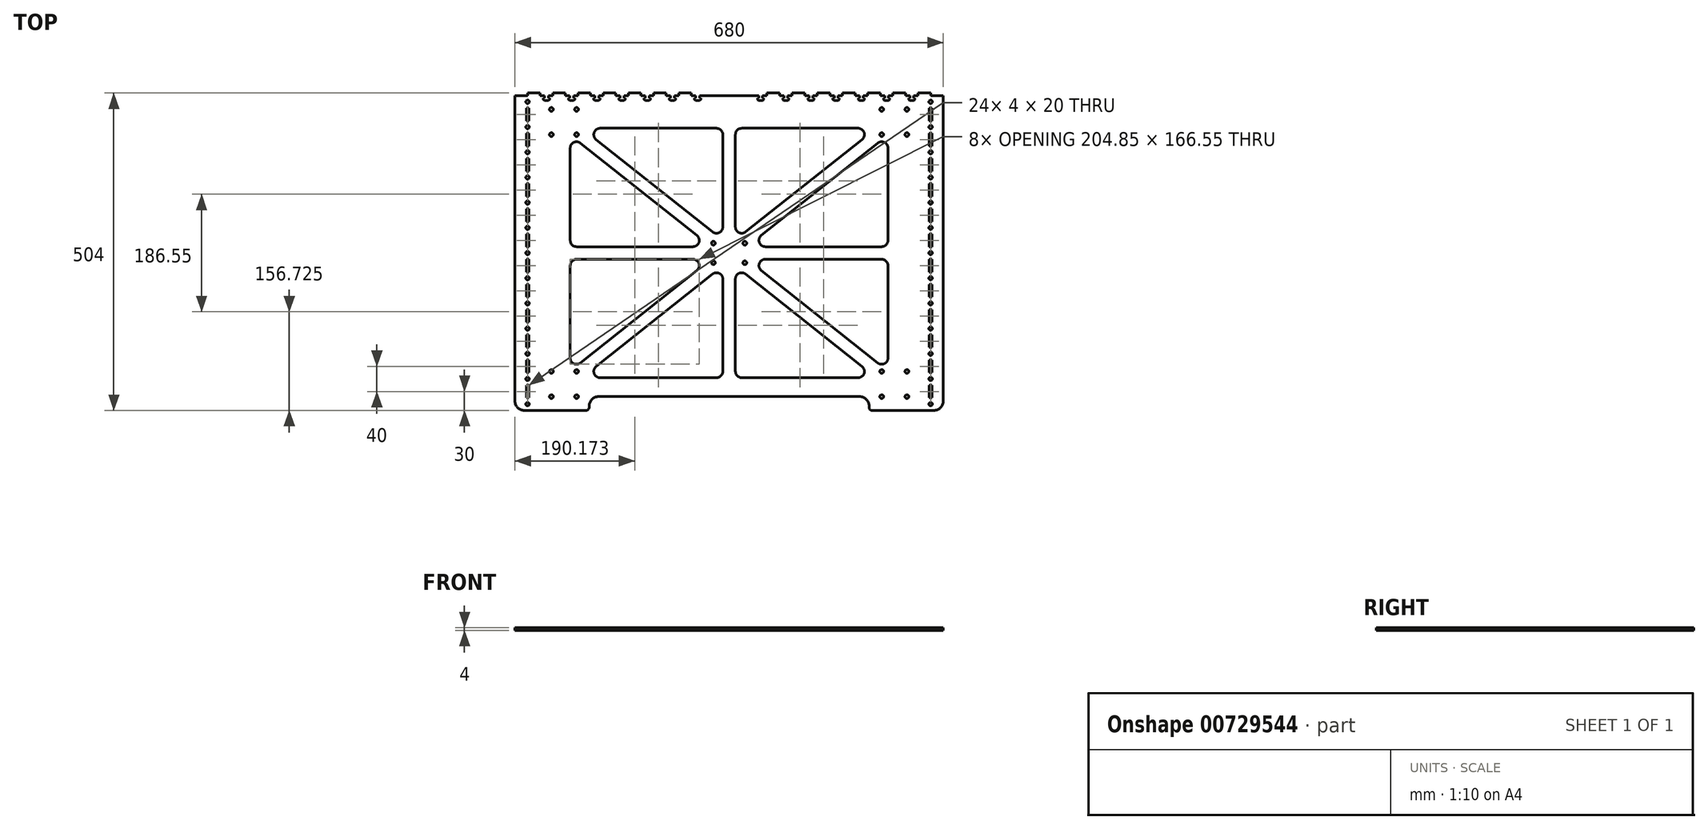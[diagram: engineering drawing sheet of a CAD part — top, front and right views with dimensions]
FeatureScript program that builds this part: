
annotation { "Feature Type Name" : "Feature", "Feature Type Description" : "" }
export const myFeature = defineFeature(function(context is Context, id is Id, definition is map)
    precondition{}
    {
        {
            var Q0;
            Q0=qCreatedBy(makeId("Top.planeOp"),FACE);
            var sketch = newSketch(context, id + "F0", { "sketchPlane" : qUnion([Q0])});
            skLineSegment(sketch, "E0.bottom", {"start": v(-340, 250) * mm, "end": v(-320, 250) * mm});
            skLineSegment(sketch, "E0.top", {"start": v(-325, -250) * mm, "end": v(-262.25, -250) * mm});
            skLineSegment(sketch, "E0.left", {"start": v(-340, 250) * mm, "end": v(-340, -235) * mm});
            skLineSegment(sketch, "E0.right", {"start": v(340, 250) * mm, "end": v(340, -235) * mm});
            skPoint(sketch, "E0.middle", {"position": v(0, 0) * mm});
            skLineSegment(sketch, "E1", {"start": v(-262.25, 250) * mm, "end": v(-262.25, -250) * mm, "construction": true});
            skLineSegment(sketch, "E2", {"start": v(262.25, 250) * mm, "end": v(262.25, -250) * mm, "construction": true});
            skLineSegment(sketch, "E3", {"start": v(0, -250) * mm, "end": v(0, 250) * mm, "construction": true});
            skLineSegment(sketch, "E4", {"start": v(340, 0) * mm, "end": v(-340, 0) * mm, "construction": true});
            skLineSegment(sketch, "E5.bottom", {"start": v(-282.25, -188) * mm, "end": v(-242.25, -188) * mm, "construction": true});
            skLineSegment(sketch, "E5.top", {"start": v(-282.25, -228) * mm, "end": v(-242.25, -228) * mm, "construction": true});
            skLineSegment(sketch, "E5.left", {"start": v(-282.25, -188) * mm, "end": v(-282.25, -228) * mm, "construction": true});
            skLineSegment(sketch, "E5.right", {"start": v(-242.25, -188) * mm, "end": v(-242.25, -228) * mm, "construction": true});
            skPoint(sketch, "E5.middle", {"position": v(-262.25, -208) * mm});
            skCircle(sketch, "E6", {"center": v(-242.25, -188) * mm, "radius": 3 * mm});
            skCircle(sketch, "E7.MirrorC", {"center": v(-282.25, -188) * mm, "radius": 3 * mm});
            skLineSegment(sketch, "E8", {"start": v(-282.25, -208) * mm, "end": v(262.25, -208) * mm, "construction": true});
            skCircle(sketch, "E9.MirrorC", {"center": v(-242.25, -228) * mm, "radius": 3 * mm});
            skCircle(sketch, "E10.MirrorC", {"center": v(-282.25, -228) * mm, "radius": 3 * mm});
            skCircle(sketch, "E11.MirrorC", {"center": v(-282.25, 188) * mm, "radius": 3 * mm});
            skCircle(sketch, "E12.MirrorC", {"center": v(-242.25, 188) * mm, "radius": 3 * mm});
            skCircle(sketch, "E13.MirrorC", {"center": v(-282.25, 228) * mm, "radius": 3 * mm});
            skCircle(sketch, "E14.MirrorC", {"center": v(-242.25, 228) * mm, "radius": 3 * mm});
            skCircle(sketch, "E15.MirrorC", {"center": v(282.25, 228) * mm, "radius": 3 * mm});
            skCircle(sketch, "E16.MirrorC", {"center": v(282.25, 188) * mm, "radius": 3 * mm});
            skCircle(sketch, "E17.MirrorC", {"center": v(242.25, 228) * mm, "radius": 3 * mm});
            skCircle(sketch, "E18.MirrorC", {"center": v(242.25, 188) * mm, "radius": 3 * mm});
            skCircle(sketch, "E19.MirrorC", {"center": v(282.25, -188) * mm, "radius": 3 * mm});
            skCircle(sketch, "E20.MirrorC", {"center": v(242.25, -188) * mm, "radius": 3 * mm});
            skCircle(sketch, "E21.MirrorC", {"center": v(242.25, -228) * mm, "radius": 3 * mm});
            skCircle(sketch, "E22.MirrorC", {"center": v(282.25, -228) * mm, "radius": 3 * mm});
            skPoint(sketch, "E23.visualSharp", {"position": v(-340, 250) * mm});
            skPoint(sketch, "E24.visualSharp", {"position": v(340, -250) * mm});
            skArc(sketch, "E24.filletArc", {"start": v(325, -250) * mm, "mid": v(335.6, -245.6) * mm, "end": v(340, -235) * mm});
            skPoint(sketch, "E25.visualSharp", {"position": v(340, 250) * mm});
            skPoint(sketch, "E26.visualSharp", {"position": v(-340, -250) * mm});
            skArc(sketch, "E26.filletArc", {"start": v(-340, -235) * mm, "mid": v(-335.6, -245.6) * mm, "end": v(-325, -250) * mm});
            skLineSegment(sketch, "E27.bottom", {"start": v(25, 15.5) * mm, "end": v(-25, 15.5) * mm, "construction": true});
            skLineSegment(sketch, "E27.top", {"start": v(25, -15.5) * mm, "end": v(-25, -15.5) * mm, "construction": true});
            skLineSegment(sketch, "E27.left", {"start": v(25, 15.5) * mm, "end": v(25, -15.5) * mm, "construction": true});
            skLineSegment(sketch, "E27.right", {"start": v(-25, 15.5) * mm, "end": v(-25, -15.5) * mm, "construction": true});
            skCircle(sketch, "E28", {"center": v(25, 15.5) * mm, "radius": 3 * mm});
            skLineSegment(sketch, "E29", {"start": v(25, 0) * mm, "end": v(0, 0) * mm, "construction": true});
            skCircle(sketch, "E30.MirrorC", {"center": v(25, -15.5) * mm, "radius": 3 * mm});
            skCircle(sketch, "E31.MirrorC", {"center": v(-25, 15.5) * mm, "radius": 3 * mm});
            skCircle(sketch, "E32.MirrorC", {"center": v(-25, -15.5) * mm, "radius": 3 * mm});
            skLineSegment(sketch, "E33", {"start": v(-262.25, -208) * mm, "end": v(0, 0) * mm, "construction": true});
            skLineSegment(sketch, "E34", {"start": v(-242.25, -10) * mm, "end": v(-57.4, -10) * mm});
            skLineSegment(sketch, "E35", {"start": v(-51.19, -27.83) * mm, "end": v(-236.04, -174.45) * mm});
            skLineSegment(sketch, "E36", {"start": v(-252.25, -166.61) * mm, "end": v(-252.25, -20) * mm});
            skPoint(sketch, "E37.visualSharp", {"position": v(-252.25, -10) * mm});
            skArc(sketch, "E37.filletArc", {"start": v(-242.25, -10) * mm, "mid": v(-249.32, -12.93) * mm, "end": v(-252.25, -20) * mm});
            skPoint(sketch, "E38.visualSharp", {"position": v(-252.25, -187.3) * mm});
            skArc(sketch, "E38.filletArc", {"start": v(-252.25, -166.61) * mm, "mid": v(-246.6, -175.61) * mm, "end": v(-236.04, -174.45) * mm});
            skPoint(sketch, "E39.visualSharp", {"position": v(-28.7, -10) * mm});
            skArc(sketch, "E39.filletArc", {"start": v(-51.19, -27.83) * mm, "mid": v(-47.96, -16.7) * mm, "end": v(-57.4, -10) * mm});
            skPoint(sketch, "E40.orphan", {"position": v(-242.25, -208) * mm});
            skLineSegment(sketch, "E41", {"start": v(-320, 250) * mm, "end": v(-320, -250) * mm, "construction": true});
            skLineSegment(sketch, "E42.bottom", {"start": v(-318, 210) * mm, "end": v(-322, 210) * mm});
            skLineSegment(sketch, "E42.top", {"start": v(-318, 230) * mm, "end": v(-322, 230) * mm});
            skLineSegment(sketch, "E42.left", {"start": v(-318, 210) * mm, "end": v(-318, 230) * mm});
            skLineSegment(sketch, "E42.right", {"start": v(-322, 210) * mm, "end": v(-322, 230) * mm});
            skPoint(sketch, "E42.middle", {"position": v(-320, 220) * mm});
            skCircle(sketch, "E43", {"center": v(-320, 240) * mm, "radius": 2.75 * mm});
            skCircle(sketch, "E44.0.1.0", {"center": v(-320, 200) * mm, "radius": 2.75 * mm});
            skLineSegment(sketch, "E44.0.1.1", {"start": v(-322, 170) * mm, "end": v(-322, 190) * mm});
            skLineSegment(sketch, "E44.0.1.2", {"start": v(-318, 190) * mm, "end": v(-322, 190) * mm});
            skPoint(sketch, "E44.0.1.3", {"position": v(-320, 180) * mm});
            skLineSegment(sketch, "E44.0.1.4", {"start": v(-318, 170) * mm, "end": v(-318, 190) * mm});
            skLineSegment(sketch, "E44.0.1.5", {"start": v(-318, 170) * mm, "end": v(-322, 170) * mm});
            skCircle(sketch, "E44.0.2.0", {"center": v(-320, 160) * mm, "radius": 2.75 * mm});
            skLineSegment(sketch, "E44.0.2.1", {"start": v(-322, 130) * mm, "end": v(-322, 150) * mm});
            skLineSegment(sketch, "E44.0.2.2", {"start": v(-318, 150) * mm, "end": v(-322, 150) * mm});
            skPoint(sketch, "E44.0.2.3", {"position": v(-320, 140) * mm});
            skLineSegment(sketch, "E44.0.2.4", {"start": v(-318, 130) * mm, "end": v(-318, 150) * mm});
            skLineSegment(sketch, "E44.0.2.5", {"start": v(-318, 130) * mm, "end": v(-322, 130) * mm});
            skCircle(sketch, "E44.0.3.0", {"center": v(-320, 120) * mm, "radius": 2.75 * mm});
            skLineSegment(sketch, "E44.0.3.1", {"start": v(-322, 90) * mm, "end": v(-322, 110) * mm});
            skLineSegment(sketch, "E44.0.3.2", {"start": v(-318, 110) * mm, "end": v(-322, 110) * mm});
            skPoint(sketch, "E44.0.3.3", {"position": v(-320, 100) * mm});
            skLineSegment(sketch, "E44.0.3.4", {"start": v(-318, 90) * mm, "end": v(-318, 110) * mm});
            skLineSegment(sketch, "E44.0.3.5", {"start": v(-318, 90) * mm, "end": v(-322, 90) * mm});
            skCircle(sketch, "E44.0.4.0", {"center": v(-320, 80) * mm, "radius": 2.75 * mm});
            skLineSegment(sketch, "E44.0.4.1", {"start": v(-322, 50) * mm, "end": v(-322, 70) * mm});
            skLineSegment(sketch, "E44.0.4.2", {"start": v(-318, 70) * mm, "end": v(-322, 70) * mm});
            skPoint(sketch, "E44.0.4.3", {"position": v(-320, 60) * mm});
            skLineSegment(sketch, "E44.0.4.4", {"start": v(-318, 50) * mm, "end": v(-318, 70) * mm});
            skLineSegment(sketch, "E44.0.4.5", {"start": v(-318, 50) * mm, "end": v(-322, 50) * mm});
            skLineSegment(sketch, "E44.direction1", {"start": v(-320, 240) * mm, "end": v(-280, 240) * mm, "construction": true});
            skLineSegment(sketch, "E44.direction2", {"start": v(-320, 240) * mm, "end": v(-320, 200) * mm, "construction": true});
            skLineSegment(sketch, "E45.top", {"start": v(-320, 254) * mm, "end": v(-300, 254) * mm});
            skLineSegment(sketch, "E45.left", {"start": v(-320, 250) * mm, "end": v(-320, 254) * mm});
            skLineSegment(sketch, "E45.right", {"start": v(-300, 250) * mm, "end": v(-300, 254) * mm});
            skLineSegment(sketch, "E46.trimOffspring", {"start": v(-300, 250) * mm, "end": v(-293, 250) * mm});
            skLineSegment(sketch, "E47.MirrorCS", {"start": v(340, 250) * mm, "end": v(320, 250) * mm});
            skLineSegment(sketch, "E48.MirrorCS", {"start": v(320, 250) * mm, "end": v(320, -250) * mm, "construction": true});
            skPoint(sketch, "E49.orphan", {"position": v(0, 250) * mm});
            skPoint(sketch, "E50.orphan", {"position": v(-262.25, 250) * mm});
            skLineSegment(sketch, "E51", {"start": v(-26.21, -33.55) * mm, "end": v(-211.06, -180.17) * mm});
            skLineSegment(sketch, "E52", {"start": v(-204.85, -198) * mm, "end": v(-20, -198) * mm});
            skLineSegment(sketch, "E53", {"start": v(-10, -188) * mm, "end": v(-10, -41.39) * mm});
            skPoint(sketch, "E54.visualSharp", {"position": v(-10, -20.7) * mm});
            skArc(sketch, "E54.filletArc", {"start": v(-10, -41.39) * mm, "mid": v(-15.65, -32.39) * mm, "end": v(-26.21, -33.55) * mm});
            skPoint(sketch, "E55.visualSharp", {"position": v(-233.55, -198) * mm});
            skArc(sketch, "E55.filletArc", {"start": v(-211.06, -180.17) * mm, "mid": v(-214.3, -191.3) * mm, "end": v(-204.85, -198) * mm});
            skPoint(sketch, "E56.visualSharp", {"position": v(-10, -198) * mm});
            skArc(sketch, "E56.filletArc", {"start": v(-20, -198) * mm, "mid": v(-12.93, -195.07) * mm, "end": v(-10, -188) * mm});
            skLineSegment(sketch, "E57.MirrorCS", {"start": v(10, -188) * mm, "end": v(10, -41.39) * mm});
            skArc(sketch, "E58.MirrorCS", {"start": v(10, -41.39) * mm, "mid": v(15.65, -32.39) * mm, "end": v(26.21, -33.55) * mm});
            skArc(sketch, "E59.MirrorCS", {"start": v(20, -198) * mm, "mid": v(12.93, -195.07) * mm, "end": v(10, -188) * mm});
            skLineSegment(sketch, "E60.MirrorCS", {"start": v(204.85, -198) * mm, "end": v(20, -198) * mm});
            skArc(sketch, "E61.MirrorCS", {"start": v(211.06, -180.17) * mm, "mid": v(214.3, -191.3) * mm, "end": v(204.85, -198) * mm});
            skLineSegment(sketch, "E62.MirrorCS", {"start": v(26.21, -33.55) * mm, "end": v(211.06, -180.17) * mm});
            skLineSegment(sketch, "E63.MirrorCS", {"start": v(51.19, -27.83) * mm, "end": v(236.04, -174.45) * mm});
            skArc(sketch, "E64.MirrorCS", {"start": v(51.19, -27.83) * mm, "mid": v(47.96, -16.7) * mm, "end": v(57.4, -10) * mm});
            skLineSegment(sketch, "E65.MirrorCS", {"start": v(242.25, -10) * mm, "end": v(57.4, -10) * mm});
            skArc(sketch, "E66.MirrorCS", {"start": v(242.25, -10) * mm, "mid": v(249.32, -12.93) * mm, "end": v(252.25, -20) * mm});
            skLineSegment(sketch, "E67.MirrorCS", {"start": v(252.25, -166.61) * mm, "end": v(252.25, -20) * mm});
            skArc(sketch, "E68.MirrorCS", {"start": v(252.25, -166.61) * mm, "mid": v(246.6, -175.61) * mm, "end": v(236.04, -174.45) * mm});
            skLineSegment(sketch, "E69.MirrorCS", {"start": v(-242.25, 10) * mm, "end": v(-57.4, 10) * mm});
            skArc(sketch, "E70.MirrorCS", {"start": v(-51.19, 27.83) * mm, "mid": v(-47.96, 16.7) * mm, "end": v(-57.4, 10) * mm});
            skLineSegment(sketch, "E71.MirrorCS", {"start": v(-51.19, 27.83) * mm, "end": v(-236.04, 174.45) * mm});
            skArc(sketch, "E72.MirrorCS", {"start": v(-252.25, 166.61) * mm, "mid": v(-246.6, 175.61) * mm, "end": v(-236.04, 174.45) * mm});
            skLineSegment(sketch, "E73.MirrorCS", {"start": v(-252.25, 166.61) * mm, "end": v(-252.25, 20) * mm});
            skLineSegment(sketch, "E74.MirrorCS", {"start": v(-26.21, 33.55) * mm, "end": v(-211.06, 180.17) * mm});
            skArc(sketch, "E75.MirrorCS", {"start": v(-10, 41.39) * mm, "mid": v(-15.65, 32.39) * mm, "end": v(-26.21, 33.55) * mm});
            skLineSegment(sketch, "E76.MirrorCS", {"start": v(-10, 188) * mm, "end": v(-10, 41.39) * mm});
            skArc(sketch, "E77.MirrorCS", {"start": v(-20, 198) * mm, "mid": v(-12.93, 195.07) * mm, "end": v(-10, 188) * mm});
            skLineSegment(sketch, "E78.MirrorCS", {"start": v(-204.85, 198) * mm, "end": v(-20, 198) * mm});
            skArc(sketch, "E79.MirrorCS", {"start": v(-211.06, 180.17) * mm, "mid": v(-214.3, 191.3) * mm, "end": v(-204.85, 198) * mm});
            skArc(sketch, "E80.MirrorCS", {"start": v(10, 41.39) * mm, "mid": v(15.65, 32.39) * mm, "end": v(26.21, 33.55) * mm});
            skLineSegment(sketch, "E81.MirrorCS", {"start": v(26.21, 33.55) * mm, "end": v(211.06, 180.17) * mm});
            skArc(sketch, "E82.MirrorCS", {"start": v(211.06, 180.17) * mm, "mid": v(214.3, 191.3) * mm, "end": v(204.85, 198) * mm});
            skLineSegment(sketch, "E83.MirrorCS", {"start": v(204.85, 198) * mm, "end": v(20, 198) * mm});
            skArc(sketch, "E84.MirrorCS", {"start": v(20, 198) * mm, "mid": v(12.93, 195.07) * mm, "end": v(10, 188) * mm});
            skLineSegment(sketch, "E85.MirrorCS", {"start": v(10, 188) * mm, "end": v(10, 41.39) * mm});
            skArc(sketch, "E86.MirrorCS", {"start": v(51.19, 27.83) * mm, "mid": v(47.96, 16.7) * mm, "end": v(57.4, 10) * mm});
            skLineSegment(sketch, "E87.MirrorCS", {"start": v(242.25, 10) * mm, "end": v(57.4, 10) * mm});
            skArc(sketch, "E88.MirrorCS", {"start": v(242.25, 10) * mm, "mid": v(249.32, 12.93) * mm, "end": v(252.25, 20) * mm});
            skLineSegment(sketch, "E89.MirrorCS", {"start": v(252.25, 166.61) * mm, "end": v(252.25, 20) * mm});
            skArc(sketch, "E90.MirrorCS", {"start": v(252.25, 166.61) * mm, "mid": v(246.6, 175.61) * mm, "end": v(236.04, 174.45) * mm});
            skLineSegment(sketch, "E91.MirrorCS", {"start": v(51.19, 27.83) * mm, "end": v(236.04, 174.45) * mm});
            skArc(sketch, "E92.MirrorCS", {"start": v(-242.25, 10) * mm, "mid": v(-249.32, 12.93) * mm, "end": v(-252.25, 20) * mm});
            skCircle(sketch, "E93.0.0.5", {"center": v(-320, 40) * mm, "radius": 2.75 * mm});
            skLineSegment(sketch, "E93.2.0.5", {"start": v(-322, 10) * mm, "end": v(-322, 30) * mm});
            skLineSegment(sketch, "E93.5.0.5", {"start": v(-318, 30) * mm, "end": v(-322, 30) * mm});
            skPoint(sketch, "E93.8.0.5", {"position": v(-320, 20) * mm});
            skLineSegment(sketch, "E93.9.0.5", {"start": v(-318, 10) * mm, "end": v(-318, 30) * mm});
            skLineSegment(sketch, "E93.12.0.5", {"start": v(-318, 10) * mm, "end": v(-322, 10) * mm});
            skCircle(sketch, "E93.0.0.6", {"center": v(-320, 0) * mm, "radius": 2.75 * mm});
            skLineSegment(sketch, "E93.2.0.6", {"start": v(-322, -30) * mm, "end": v(-322, -10) * mm});
            skLineSegment(sketch, "E93.5.0.6", {"start": v(-318, -10) * mm, "end": v(-322, -10) * mm});
            skPoint(sketch, "E93.8.0.6", {"position": v(-320, -20) * mm});
            skLineSegment(sketch, "E93.9.0.6", {"start": v(-318, -30) * mm, "end": v(-318, -10) * mm});
            skLineSegment(sketch, "E93.12.0.6", {"start": v(-318, -30) * mm, "end": v(-322, -30) * mm});
            skCircle(sketch, "E93.0.0.7", {"center": v(-320, -40) * mm, "radius": 2.75 * mm});
            skLineSegment(sketch, "E93.2.0.7", {"start": v(-322, -70) * mm, "end": v(-322, -50) * mm});
            skLineSegment(sketch, "E93.5.0.7", {"start": v(-318, -50) * mm, "end": v(-322, -50) * mm});
            skPoint(sketch, "E93.8.0.7", {"position": v(-320, -60) * mm});
            skLineSegment(sketch, "E93.9.0.7", {"start": v(-318, -70) * mm, "end": v(-318, -50) * mm});
            skLineSegment(sketch, "E93.12.0.7", {"start": v(-318, -70) * mm, "end": v(-322, -70) * mm});
            skCircle(sketch, "E93.0.0.8", {"center": v(-320, -80) * mm, "radius": 2.75 * mm});
            skLineSegment(sketch, "E93.2.0.8", {"start": v(-322, -110) * mm, "end": v(-322, -90) * mm});
            skLineSegment(sketch, "E93.5.0.8", {"start": v(-318, -90) * mm, "end": v(-322, -90) * mm});
            skPoint(sketch, "E93.8.0.8", {"position": v(-320, -100) * mm});
            skLineSegment(sketch, "E93.9.0.8", {"start": v(-318, -110) * mm, "end": v(-318, -90) * mm});
            skLineSegment(sketch, "E93.12.0.8", {"start": v(-318, -110) * mm, "end": v(-322, -110) * mm});
            skCircle(sketch, "E93.0.0.9", {"center": v(-320, -120) * mm, "radius": 2.75 * mm});
            skLineSegment(sketch, "E93.2.0.9", {"start": v(-322, -150) * mm, "end": v(-322, -130) * mm});
            skLineSegment(sketch, "E93.5.0.9", {"start": v(-318, -130) * mm, "end": v(-322, -130) * mm});
            skPoint(sketch, "E93.8.0.9", {"position": v(-320, -140) * mm});
            skLineSegment(sketch, "E93.9.0.9", {"start": v(-318, -150) * mm, "end": v(-318, -130) * mm});
            skLineSegment(sketch, "E93.12.0.9", {"start": v(-318, -150) * mm, "end": v(-322, -150) * mm});
            skCircle(sketch, "E93.0.0.10", {"center": v(-320, -160) * mm, "radius": 2.75 * mm});
            skLineSegment(sketch, "E93.2.0.10", {"start": v(-322, -190) * mm, "end": v(-322, -170) * mm});
            skLineSegment(sketch, "E93.5.0.10", {"start": v(-318, -170) * mm, "end": v(-322, -170) * mm});
            skPoint(sketch, "E93.8.0.10", {"position": v(-320, -180) * mm});
            skLineSegment(sketch, "E93.9.0.10", {"start": v(-318, -190) * mm, "end": v(-318, -170) * mm});
            skLineSegment(sketch, "E93.12.0.10", {"start": v(-318, -190) * mm, "end": v(-322, -190) * mm});
            skCircle(sketch, "E93.0.0.11", {"center": v(-320, -200) * mm, "radius": 2.75 * mm});
            skLineSegment(sketch, "E93.2.0.11", {"start": v(-322, -230) * mm, "end": v(-322, -210) * mm});
            skLineSegment(sketch, "E93.5.0.11", {"start": v(-318, -210) * mm, "end": v(-322, -210) * mm});
            skPoint(sketch, "E93.8.0.11", {"position": v(-320, -220) * mm});
            skLineSegment(sketch, "E93.9.0.11", {"start": v(-318, -230) * mm, "end": v(-318, -210) * mm});
            skLineSegment(sketch, "E93.12.0.11", {"start": v(-318, -230) * mm, "end": v(-322, -230) * mm});
            skCircle(sketch, "E94", {"center": v(-320, -240) * mm, "radius": 2.75 * mm});
            skLineSegment(sketch, "E95.MirrorCS", {"start": v(318, -190) * mm, "end": v(322, -190) * mm});
            skLineSegment(sketch, "E96.MirrorCS", {"start": v(318, -210) * mm, "end": v(322, -210) * mm});
            skLineSegment(sketch, "E97.MirrorCS", {"start": v(318, -230) * mm, "end": v(322, -230) * mm});
            skLineSegment(sketch, "E98.MirrorCS", {"start": v(318, -170) * mm, "end": v(322, -170) * mm});
            skLineSegment(sketch, "E99.MirrorCS", {"start": v(318, -150) * mm, "end": v(322, -150) * mm});
            skLineSegment(sketch, "E100.MirrorCS", {"start": v(318, -130) * mm, "end": v(322, -130) * mm});
            skCircle(sketch, "E101.MirrorC", {"center": v(320, -160) * mm, "radius": 2.75 * mm});
            skPoint(sketch, "E102.MirrorP", {"position": v(320, -140) * mm});
            skLineSegment(sketch, "E103.MirrorCS", {"start": v(322, -230) * mm, "end": v(322, -210) * mm});
            skPoint(sketch, "E104.MirrorP", {"position": v(320, -180) * mm});
            skLineSegment(sketch, "E105.MirrorCS", {"start": v(318, -230) * mm, "end": v(318, -210) * mm});
            skPoint(sketch, "E106.MirrorP", {"position": v(320, -220) * mm});
            skCircle(sketch, "E107.MirrorC", {"center": v(320, -240) * mm, "radius": 2.75 * mm});
            skLineSegment(sketch, "E108.MirrorCS", {"start": v(322, -190) * mm, "end": v(322, -170) * mm});
            skCircle(sketch, "E109.MirrorC", {"center": v(320, -200) * mm, "radius": 2.75 * mm});
            skLineSegment(sketch, "E110.MirrorCS", {"start": v(322, -150) * mm, "end": v(322, -130) * mm});
            skLineSegment(sketch, "E111.MirrorCS", {"start": v(318, -190) * mm, "end": v(318, -170) * mm});
            skLineSegment(sketch, "E112.MirrorCS", {"start": v(318, -150) * mm, "end": v(318, -130) * mm});
            skLineSegment(sketch, "E113.MirrorCS", {"start": v(318, -90) * mm, "end": v(322, -90) * mm});
            skLineSegment(sketch, "E114.MirrorCS", {"start": v(322, 10) * mm, "end": v(322, 30) * mm});
            skLineSegment(sketch, "E115.MirrorCS", {"start": v(318, 10) * mm, "end": v(322, 10) * mm});
            skLineSegment(sketch, "E116.MirrorCS", {"start": v(318, -10) * mm, "end": v(322, -10) * mm});
            skLineSegment(sketch, "E117.MirrorCS", {"start": v(318, -70) * mm, "end": v(322, -70) * mm});
            skLineSegment(sketch, "E118.MirrorCS", {"start": v(322, -110) * mm, "end": v(322, -90) * mm});
            skLineSegment(sketch, "E119.MirrorCS", {"start": v(318, 90) * mm, "end": v(322, 90) * mm});
            skLineSegment(sketch, "E120.MirrorCS", {"start": v(322, 90) * mm, "end": v(322, 110) * mm});
            skLineSegment(sketch, "E121.MirrorCS", {"start": v(318, -50) * mm, "end": v(322, -50) * mm});
            skLineSegment(sketch, "E122.MirrorCS", {"start": v(322, -70) * mm, "end": v(322, -50) * mm});
            skLineSegment(sketch, "E123.MirrorCS", {"start": v(318, 50) * mm, "end": v(322, 50) * mm});
            skLineSegment(sketch, "E124.MirrorCS", {"start": v(318, -30) * mm, "end": v(322, -30) * mm});
            skLineSegment(sketch, "E125.MirrorCS", {"start": v(322, -30) * mm, "end": v(322, -10) * mm});
            skLineSegment(sketch, "E126.MirrorCS", {"start": v(318, 110) * mm, "end": v(322, 110) * mm});
            skLineSegment(sketch, "E127.MirrorCS", {"start": v(318, 30) * mm, "end": v(322, 30) * mm});
            skLineSegment(sketch, "E128.MirrorCS", {"start": v(318, 70) * mm, "end": v(322, 70) * mm});
            skLineSegment(sketch, "E129.MirrorCS", {"start": v(322, 50) * mm, "end": v(322, 70) * mm});
            skLineSegment(sketch, "E130.MirrorCS", {"start": v(318, -110) * mm, "end": v(322, -110) * mm});
            skLineSegment(sketch, "E131.MirrorCS", {"start": v(318, 90) * mm, "end": v(318, 110) * mm});
            skCircle(sketch, "E132.MirrorC", {"center": v(320, 120) * mm, "radius": 2.75 * mm});
            skCircle(sketch, "E133.MirrorC", {"center": v(320, -120) * mm, "radius": 2.75 * mm});
            skCircle(sketch, "E134.MirrorC", {"center": v(320, 40) * mm, "radius": 2.75 * mm});
            skLineSegment(sketch, "E135.MirrorCS", {"start": v(318, -70) * mm, "end": v(318, -50) * mm});
            skCircle(sketch, "E136.MirrorC", {"center": v(320, 80) * mm, "radius": 2.75 * mm});
            skCircle(sketch, "E137.MirrorC", {"center": v(320, 0) * mm, "radius": 2.75 * mm});
            skCircle(sketch, "E138.MirrorC", {"center": v(320, -40) * mm, "radius": 2.75 * mm});
            skLineSegment(sketch, "E139.MirrorCS", {"start": v(318, 50) * mm, "end": v(318, 70) * mm});
            skLineSegment(sketch, "E140.MirrorCS", {"start": v(318, -110) * mm, "end": v(318, -90) * mm});
            skLineSegment(sketch, "E141.MirrorCS", {"start": v(318, -30) * mm, "end": v(318, -10) * mm});
            skCircle(sketch, "E142.MirrorC", {"center": v(320, -80) * mm, "radius": 2.75 * mm});
            skLineSegment(sketch, "E143.MirrorCS", {"start": v(318, 10) * mm, "end": v(318, 30) * mm});
            skPoint(sketch, "E144.MirrorP", {"position": v(320, 100) * mm});
            skPoint(sketch, "E145.MirrorP", {"position": v(320, 20) * mm});
            skPoint(sketch, "E146.MirrorP", {"position": v(320, 60) * mm});
            skLineSegment(sketch, "E147.MirrorCS", {"start": v(-340, 0) * mm, "end": v(340, 0) * mm, "construction": true});
            skPoint(sketch, "E148.MirrorP", {"position": v(320, -100) * mm});
            skPoint(sketch, "E149.MirrorP", {"position": v(320, -20) * mm});
            skPoint(sketch, "E150.MirrorP", {"position": v(320, -60) * mm});
            skLineSegment(sketch, "E151.MirrorCS", {"start": v(318, 170) * mm, "end": v(322, 170) * mm});
            skLineSegment(sketch, "E152.MirrorCS", {"start": v(318, 190) * mm, "end": v(322, 190) * mm});
            skLineSegment(sketch, "E153.MirrorCS", {"start": v(318, 130) * mm, "end": v(322, 130) * mm});
            skLineSegment(sketch, "E154.MirrorCS", {"start": v(318, 210) * mm, "end": v(322, 210) * mm});
            skLineSegment(sketch, "E155.MirrorCS", {"start": v(318, 230) * mm, "end": v(322, 230) * mm});
            skLineSegment(sketch, "E156.MirrorCS", {"start": v(318, 150) * mm, "end": v(322, 150) * mm});
            skCircle(sketch, "E157.MirrorC", {"center": v(320, 240) * mm, "radius": 2.75 * mm});
            skLineSegment(sketch, "E158.MirrorCS", {"start": v(318, 170) * mm, "end": v(318, 190) * mm});
            skLineSegment(sketch, "E159.MirrorCS", {"start": v(322, 130) * mm, "end": v(322, 150) * mm});
            skLineSegment(sketch, "E160.MirrorCS", {"start": v(318, 130) * mm, "end": v(318, 150) * mm});
            skPoint(sketch, "E161.MirrorP", {"position": v(320, 180) * mm});
            skCircle(sketch, "E162.MirrorC", {"center": v(320, 200) * mm, "radius": 2.75 * mm});
            skPoint(sketch, "E163.MirrorP", {"position": v(320, 140) * mm});
            skCircle(sketch, "E164.MirrorC", {"center": v(320, 160) * mm, "radius": 2.75 * mm});
            skLineSegment(sketch, "E165.MirrorCS", {"start": v(318, 210) * mm, "end": v(318, 230) * mm});
            skLineSegment(sketch, "E166.MirrorCS", {"start": v(322, 170) * mm, "end": v(322, 190) * mm});
            skLineSegment(sketch, "E167.MirrorCS", {"start": v(322, 210) * mm, "end": v(322, 230) * mm});
            skLineSegment(sketch, "E168.top", {"start": v(-207.25, -228) * mm, "end": v(207.25, -228) * mm});
            skLineSegment(sketch, "E168.left", {"start": v(-222.25, -245) * mm, "end": v(-222.25, -243) * mm});
            skLineSegment(sketch, "E168.right", {"start": v(222.25, -245) * mm, "end": v(222.25, -243) * mm});
            skPoint(sketch, "E169.visualSharp", {"position": v(-222.25, -228) * mm});
            skArc(sketch, "E169.filletArc", {"start": v(-207.25, -228) * mm, "mid": v(-217.86, -232.4) * mm, "end": v(-222.25, -243) * mm});
            skPoint(sketch, "E170.visualSharp", {"position": v(222.25, -228) * mm});
            skArc(sketch, "E170.filletArc", {"start": v(222.25, -243) * mm, "mid": v(217.86, -232.4) * mm, "end": v(207.25, -228) * mm});
            skLineSegment(sketch, "E171.trimOffspring", {"start": v(227.25, -250) * mm, "end": v(325, -250) * mm});
            skLineSegment(sketch, "E172", {"start": v(-262.25, -250) * mm, "end": v(-227.25, -250) * mm});
            skPoint(sketch, "E173.visualSharp", {"position": v(-222.25, -250) * mm});
            skArc(sketch, "E173.filletArc", {"start": v(-227.25, -250) * mm, "mid": v(-223.71, -248.54) * mm, "end": v(-222.25, -245) * mm});
            skPoint(sketch, "E174.visualSharp", {"position": v(222.25, -250) * mm});
            skArc(sketch, "E174.filletArc", {"start": v(222.25, -245) * mm, "mid": v(223.71, -248.54) * mm, "end": v(227.25, -250) * mm});
            skLineSegment(sketch, "E175", {"start": v(-290, 242) * mm, "end": v(-290, 250) * mm, "construction": true});
            skLineSegment(sketch, "E176", {"start": v(-290, 242) * mm, "end": v(-286.6, 242) * mm});
            skLineSegment(sketch, "E177", {"start": v(-286.6, 242) * mm, "end": v(-285, 243.6) * mm});
            skLineSegment(sketch, "E178", {"start": v(-285, 243.6) * mm, "end": v(-285, 246) * mm});
            skLineSegment(sketch, "E179", {"start": v(-285, 246) * mm, "end": v(-287, 246) * mm});
            skLineSegment(sketch, "E180", {"start": v(-287, 246) * mm, "end": v(-287, 250) * mm});
            skLineSegment(sketch, "E181.MirrorCS", {"start": v(-290, 242) * mm, "end": v(-293.4, 242) * mm});
            skLineSegment(sketch, "E182.MirrorCS", {"start": v(-293, 246) * mm, "end": v(-293, 250) * mm});
            skLineSegment(sketch, "E183.MirrorCS", {"start": v(-295, 246) * mm, "end": v(-293, 246) * mm});
            skLineSegment(sketch, "E184.MirrorCS", {"start": v(-295, 243.6) * mm, "end": v(-295, 246) * mm});
            skLineSegment(sketch, "E185.MirrorCS", {"start": v(-293.4, 242) * mm, "end": v(-295, 243.6) * mm});
            skLineSegment(sketch, "E186", {"start": v(-287, 250) * mm, "end": v(-280, 250) * mm});
            skLineSegment(sketch, "E187.1.0.0", {"start": v(-280, 250) * mm, "end": v(-280, 254) * mm});
            skLineSegment(sketch, "E187.1.0.1", {"start": v(-280, 254) * mm, "end": v(-260, 254) * mm});
            skLineSegment(sketch, "E187.1.0.2", {"start": v(-260, 250) * mm, "end": v(-260, 254) * mm});
            skLineSegment(sketch, "E187.1.0.3", {"start": v(-260, 250) * mm, "end": v(-253, 250) * mm});
            skLineSegment(sketch, "E187.1.0.4", {"start": v(-253, 246) * mm, "end": v(-253, 250) * mm});
            skLineSegment(sketch, "E187.1.0.5", {"start": v(-255, 246) * mm, "end": v(-253, 246) * mm});
            skLineSegment(sketch, "E187.1.0.6", {"start": v(-255, 243.6) * mm, "end": v(-255, 246) * mm});
            skLineSegment(sketch, "E187.1.0.7", {"start": v(-253.4, 242) * mm, "end": v(-255, 243.6) * mm});
            skLineSegment(sketch, "E187.1.0.8", {"start": v(-250, 242) * mm, "end": v(-253.4, 242) * mm});
            skLineSegment(sketch, "E187.1.0.9", {"start": v(-250, 242) * mm, "end": v(-246.6, 242) * mm});
            skLineSegment(sketch, "E187.1.0.10", {"start": v(-246.6, 242) * mm, "end": v(-245, 243.6) * mm});
            skLineSegment(sketch, "E187.1.0.11", {"start": v(-245, 243.6) * mm, "end": v(-245, 246) * mm});
            skLineSegment(sketch, "E187.1.0.12", {"start": v(-245, 246) * mm, "end": v(-247, 246) * mm});
            skLineSegment(sketch, "E187.1.0.13", {"start": v(-247, 246) * mm, "end": v(-247, 250) * mm});
            skLineSegment(sketch, "E187.1.0.14", {"start": v(-247, 250) * mm, "end": v(-240, 250) * mm});
            skLineSegment(sketch, "E187.2.0.0", {"start": v(-240, 250) * mm, "end": v(-240, 254) * mm});
            skLineSegment(sketch, "E187.2.0.1", {"start": v(-240, 254) * mm, "end": v(-220, 254) * mm});
            skLineSegment(sketch, "E187.2.0.2", {"start": v(-220, 250) * mm, "end": v(-220, 254) * mm});
            skLineSegment(sketch, "E187.2.0.3", {"start": v(-220, 250) * mm, "end": v(-213, 250) * mm});
            skLineSegment(sketch, "E187.2.0.4", {"start": v(-213, 246) * mm, "end": v(-213, 250) * mm});
            skLineSegment(sketch, "E187.2.0.5", {"start": v(-215, 246) * mm, "end": v(-213, 246) * mm});
            skLineSegment(sketch, "E187.2.0.6", {"start": v(-215, 243.6) * mm, "end": v(-215, 246) * mm});
            skLineSegment(sketch, "E187.2.0.7", {"start": v(-213.4, 242) * mm, "end": v(-215, 243.6) * mm});
            skLineSegment(sketch, "E187.2.0.8", {"start": v(-210, 242) * mm, "end": v(-213.4, 242) * mm});
            skLineSegment(sketch, "E187.2.0.9", {"start": v(-210, 242) * mm, "end": v(-206.6, 242) * mm});
            skLineSegment(sketch, "E187.2.0.10", {"start": v(-206.6, 242) * mm, "end": v(-205, 243.6) * mm});
            skLineSegment(sketch, "E187.2.0.11", {"start": v(-205, 243.6) * mm, "end": v(-205, 246) * mm});
            skLineSegment(sketch, "E187.2.0.12", {"start": v(-205, 246) * mm, "end": v(-207, 246) * mm});
            skLineSegment(sketch, "E187.2.0.13", {"start": v(-207, 246) * mm, "end": v(-207, 250) * mm});
            skLineSegment(sketch, "E187.2.0.14", {"start": v(-207, 250) * mm, "end": v(-200, 250) * mm});
            skLineSegment(sketch, "E187.3.0.0", {"start": v(-200, 250) * mm, "end": v(-200, 254) * mm});
            skLineSegment(sketch, "E187.3.0.1", {"start": v(-200, 254) * mm, "end": v(-180, 254) * mm});
            skLineSegment(sketch, "E187.3.0.2", {"start": v(-180, 250) * mm, "end": v(-180, 254) * mm});
            skLineSegment(sketch, "E187.3.0.3", {"start": v(-180, 250) * mm, "end": v(-173, 250) * mm});
            skLineSegment(sketch, "E187.3.0.4", {"start": v(-173, 246) * mm, "end": v(-173, 250) * mm});
            skLineSegment(sketch, "E187.3.0.5", {"start": v(-175, 246) * mm, "end": v(-173, 246) * mm});
            skLineSegment(sketch, "E187.3.0.6", {"start": v(-175, 243.6) * mm, "end": v(-175, 246) * mm});
            skLineSegment(sketch, "E187.3.0.7", {"start": v(-173.4, 242) * mm, "end": v(-175, 243.6) * mm});
            skLineSegment(sketch, "E187.3.0.8", {"start": v(-170, 242) * mm, "end": v(-173.4, 242) * mm});
            skLineSegment(sketch, "E187.3.0.9", {"start": v(-170, 242) * mm, "end": v(-166.6, 242) * mm});
            skLineSegment(sketch, "E187.3.0.10", {"start": v(-166.6, 242) * mm, "end": v(-165, 243.6) * mm});
            skLineSegment(sketch, "E187.3.0.11", {"start": v(-165, 243.6) * mm, "end": v(-165, 246) * mm});
            skLineSegment(sketch, "E187.3.0.12", {"start": v(-165, 246) * mm, "end": v(-167, 246) * mm});
            skLineSegment(sketch, "E187.3.0.13", {"start": v(-167, 246) * mm, "end": v(-167, 250) * mm});
            skLineSegment(sketch, "E187.3.0.14", {"start": v(-167, 250) * mm, "end": v(-160, 250) * mm});
            skLineSegment(sketch, "E187.4.0.0", {"start": v(-160, 250) * mm, "end": v(-160, 254) * mm});
            skLineSegment(sketch, "E187.4.0.1", {"start": v(-160, 254) * mm, "end": v(-140, 254) * mm});
            skLineSegment(sketch, "E187.4.0.2", {"start": v(-140, 250) * mm, "end": v(-140, 254) * mm});
            skLineSegment(sketch, "E187.4.0.3", {"start": v(-140, 250) * mm, "end": v(-133, 250) * mm});
            skLineSegment(sketch, "E187.4.0.4", {"start": v(-133, 246) * mm, "end": v(-133, 250) * mm});
            skLineSegment(sketch, "E187.4.0.5", {"start": v(-135, 246) * mm, "end": v(-133, 246) * mm});
            skLineSegment(sketch, "E187.4.0.6", {"start": v(-135, 243.6) * mm, "end": v(-135, 246) * mm});
            skLineSegment(sketch, "E187.4.0.7", {"start": v(-133.4, 242) * mm, "end": v(-135, 243.6) * mm});
            skLineSegment(sketch, "E187.4.0.8", {"start": v(-130, 242) * mm, "end": v(-133.4, 242) * mm});
            skLineSegment(sketch, "E187.4.0.9", {"start": v(-130, 242) * mm, "end": v(-126.6, 242) * mm});
            skLineSegment(sketch, "E187.4.0.10", {"start": v(-126.6, 242) * mm, "end": v(-125, 243.6) * mm});
            skLineSegment(sketch, "E187.4.0.11", {"start": v(-125, 243.6) * mm, "end": v(-125, 246) * mm});
            skLineSegment(sketch, "E187.4.0.12", {"start": v(-125, 246) * mm, "end": v(-127, 246) * mm});
            skLineSegment(sketch, "E187.4.0.13", {"start": v(-127, 246) * mm, "end": v(-127, 250) * mm});
            skLineSegment(sketch, "E187.4.0.14", {"start": v(-127, 250) * mm, "end": v(-120, 250) * mm});
            skLineSegment(sketch, "E187.5.0.0", {"start": v(-120, 250) * mm, "end": v(-120, 254) * mm});
            skLineSegment(sketch, "E187.5.0.1", {"start": v(-120, 254) * mm, "end": v(-100, 254) * mm});
            skLineSegment(sketch, "E187.5.0.2", {"start": v(-100, 250) * mm, "end": v(-100, 254) * mm});
            skLineSegment(sketch, "E187.5.0.3", {"start": v(-100, 250) * mm, "end": v(-93, 250) * mm});
            skLineSegment(sketch, "E187.5.0.4", {"start": v(-93, 246) * mm, "end": v(-93, 250) * mm});
            skLineSegment(sketch, "E187.5.0.5", {"start": v(-95, 246) * mm, "end": v(-93, 246) * mm});
            skLineSegment(sketch, "E187.5.0.6", {"start": v(-95, 243.6) * mm, "end": v(-95, 246) * mm});
            skLineSegment(sketch, "E187.5.0.7", {"start": v(-93.4, 242) * mm, "end": v(-95, 243.6) * mm});
            skLineSegment(sketch, "E187.5.0.8", {"start": v(-90, 242) * mm, "end": v(-93.4, 242) * mm});
            skLineSegment(sketch, "E187.5.0.9", {"start": v(-90, 242) * mm, "end": v(-86.6, 242) * mm});
            skLineSegment(sketch, "E187.5.0.10", {"start": v(-86.6, 242) * mm, "end": v(-85, 243.6) * mm});
            skLineSegment(sketch, "E187.5.0.11", {"start": v(-85, 243.6) * mm, "end": v(-85, 246) * mm});
            skLineSegment(sketch, "E187.5.0.12", {"start": v(-85, 246) * mm, "end": v(-87, 246) * mm});
            skLineSegment(sketch, "E187.5.0.13", {"start": v(-87, 246) * mm, "end": v(-87, 250) * mm});
            skLineSegment(sketch, "E187.5.0.14", {"start": v(-87, 250) * mm, "end": v(-80, 250) * mm});
            skLineSegment(sketch, "E187.6.0.0", {"start": v(-80, 250) * mm, "end": v(-80, 254) * mm});
            skLineSegment(sketch, "E187.6.0.1", {"start": v(-80, 254) * mm, "end": v(-60, 254) * mm});
            skLineSegment(sketch, "E187.6.0.2", {"start": v(-60, 250) * mm, "end": v(-60, 254) * mm});
            skLineSegment(sketch, "E187.6.0.3", {"start": v(-60, 250) * mm, "end": v(-53, 250) * mm});
            skLineSegment(sketch, "E187.6.0.4", {"start": v(-53, 246) * mm, "end": v(-53, 250) * mm});
            skLineSegment(sketch, "E187.6.0.5", {"start": v(-55, 246) * mm, "end": v(-53, 246) * mm});
            skLineSegment(sketch, "E187.6.0.6", {"start": v(-55, 243.6) * mm, "end": v(-55, 246) * mm});
            skLineSegment(sketch, "E187.6.0.7", {"start": v(-53.4, 242) * mm, "end": v(-55, 243.6) * mm});
            skLineSegment(sketch, "E187.6.0.8", {"start": v(-50, 242) * mm, "end": v(-53.4, 242) * mm});
            skLineSegment(sketch, "E187.6.0.9", {"start": v(-50, 242) * mm, "end": v(-46.6, 242) * mm});
            skLineSegment(sketch, "E187.6.0.10", {"start": v(-46.6, 242) * mm, "end": v(-45, 243.6) * mm});
            skLineSegment(sketch, "E187.6.0.11", {"start": v(-45, 243.6) * mm, "end": v(-45, 246) * mm});
            skLineSegment(sketch, "E187.6.0.12", {"start": v(-45, 246) * mm, "end": v(-47, 246) * mm});
            skLineSegment(sketch, "E187.6.0.13", {"start": v(-47, 246) * mm, "end": v(-47, 250) * mm});
            skLineSegment(sketch, "E187.6.0.14", {"start": v(-47, 250) * mm, "end": v(-40, 250) * mm});
            skLineSegment(sketch, "E187.direction1", {"start": v(-320, 250) * mm, "end": v(-280, 250) * mm, "construction": true});
            skLineSegment(sketch, "E188.MirrorCS", {"start": v(130, 242) * mm, "end": v(126.6, 242) * mm});
            skLineSegment(sketch, "E189.MirrorCS", {"start": v(290, 242) * mm, "end": v(293.4, 242) * mm});
            skLineSegment(sketch, "E190.MirrorCS", {"start": v(215, 246) * mm, "end": v(213, 246) * mm});
            skLineSegment(sketch, "E191.MirrorCS", {"start": v(286.6, 242) * mm, "end": v(285, 243.6) * mm});
            skLineSegment(sketch, "E192.MirrorCS", {"start": v(285, 243.6) * mm, "end": v(285, 246) * mm});
            skLineSegment(sketch, "E193.MirrorCS", {"start": v(255, 243.6) * mm, "end": v(255, 246) * mm});
            skLineSegment(sketch, "E194.MirrorCS", {"start": v(295, 243.6) * mm, "end": v(295, 246) * mm});
            skLineSegment(sketch, "E195.MirrorCS", {"start": v(295, 246) * mm, "end": v(293, 246) * mm});
            skLineSegment(sketch, "E196.MirrorCS", {"start": v(285, 246) * mm, "end": v(287, 246) * mm});
            skLineSegment(sketch, "E197.MirrorCS", {"start": v(290, 242) * mm, "end": v(286.6, 242) * mm});
            skLineSegment(sketch, "E198.MirrorCS", {"start": v(255, 246) * mm, "end": v(253, 246) * mm});
            skLineSegment(sketch, "E199.MirrorCS", {"start": v(135, 246) * mm, "end": v(133, 246) * mm});
            skLineSegment(sketch, "E200.MirrorCS", {"start": v(170, 242) * mm, "end": v(173.4, 242) * mm});
            skLineSegment(sketch, "E201.MirrorCS", {"start": v(170, 242) * mm, "end": v(166.6, 242) * mm});
            skLineSegment(sketch, "E202.MirrorCS", {"start": v(253.4, 242) * mm, "end": v(255, 243.6) * mm});
            skLineSegment(sketch, "E203.MirrorCS", {"start": v(253, 246) * mm, "end": v(253, 250) * mm});
            skLineSegment(sketch, "E204.MirrorCS", {"start": v(167, 246) * mm, "end": v(167, 250) * mm});
            skLineSegment(sketch, "E205.MirrorCS", {"start": v(133.4, 242) * mm, "end": v(135, 243.6) * mm});
            skLineSegment(sketch, "E206.MirrorCS", {"start": v(287, 246) * mm, "end": v(287, 250) * mm});
            skLineSegment(sketch, "E207.MirrorCS", {"start": v(165, 243.6) * mm, "end": v(165, 246) * mm});
            skLineSegment(sketch, "E208.MirrorCS", {"start": v(55, 246) * mm, "end": v(53, 246) * mm});
            skLineSegment(sketch, "E209.MirrorCS", {"start": v(165, 246) * mm, "end": v(167, 246) * mm});
            skLineSegment(sketch, "E210.MirrorCS", {"start": v(135, 243.6) * mm, "end": v(135, 246) * mm});
            skLineSegment(sketch, "E211.MirrorCS", {"start": v(215, 243.6) * mm, "end": v(215, 246) * mm});
            skLineSegment(sketch, "E212.MirrorCS", {"start": v(55, 243.6) * mm, "end": v(55, 246) * mm});
            skLineSegment(sketch, "E213.MirrorCS", {"start": v(126.6, 242) * mm, "end": v(125, 243.6) * mm});
            skLineSegment(sketch, "E214.MirrorCS", {"start": v(213, 246) * mm, "end": v(213, 250) * mm});
            skLineSegment(sketch, "E215.MirrorCS", {"start": v(175, 246) * mm, "end": v(173, 246) * mm});
            skLineSegment(sketch, "E216.MirrorCS", {"start": v(293.4, 242) * mm, "end": v(295, 243.6) * mm});
            skLineSegment(sketch, "E217.MirrorCS", {"start": v(205, 246) * mm, "end": v(207, 246) * mm});
            skLineSegment(sketch, "E218.MirrorCS", {"start": v(86.6, 242) * mm, "end": v(85, 243.6) * mm});
            skLineSegment(sketch, "E219.MirrorCS", {"start": v(175, 243.6) * mm, "end": v(175, 246) * mm});
            skLineSegment(sketch, "E220.MirrorCS", {"start": v(220, 250) * mm, "end": v(213, 250) * mm});
            skLineSegment(sketch, "E221.MirrorCS", {"start": v(205, 243.6) * mm, "end": v(205, 246) * mm});
            skLineSegment(sketch, "E222.MirrorCS", {"start": v(53, 246) * mm, "end": v(53, 250) * mm});
            skLineSegment(sketch, "E223.MirrorCS", {"start": v(85, 243.6) * mm, "end": v(85, 246) * mm});
            skLineSegment(sketch, "E224.MirrorCS", {"start": v(140, 250) * mm, "end": v(133, 250) * mm});
            skLineSegment(sketch, "E225.MirrorCS", {"start": v(260, 250) * mm, "end": v(260, 254) * mm});
            skLineSegment(sketch, "E226.MirrorCS", {"start": v(130, 242) * mm, "end": v(133.4, 242) * mm});
            skLineSegment(sketch, "E227.MirrorCS", {"start": v(213.4, 242) * mm, "end": v(215, 243.6) * mm});
            skLineSegment(sketch, "E228.MirrorCS", {"start": v(60, 250) * mm, "end": v(60, 254) * mm});
            skLineSegment(sketch, "E229.MirrorCS", {"start": v(180, 250) * mm, "end": v(180, 254) * mm});
            skLineSegment(sketch, "E230.MirrorCS", {"start": v(173, 246) * mm, "end": v(173, 250) * mm});
            skLineSegment(sketch, "E231.MirrorCS", {"start": v(95, 243.6) * mm, "end": v(95, 246) * mm});
            skLineSegment(sketch, "E232.MirrorCS", {"start": v(287, 250) * mm, "end": v(280, 250) * mm});
            skLineSegment(sketch, "E233.MirrorCS", {"start": v(46.6, 242) * mm, "end": v(45, 243.6) * mm});
            skLineSegment(sketch, "E234.MirrorCS", {"start": v(220, 250) * mm, "end": v(220, 254) * mm});
            skLineSegment(sketch, "E235.MirrorCS", {"start": v(180, 250) * mm, "end": v(173, 250) * mm});
            skLineSegment(sketch, "E236.MirrorCS", {"start": v(133, 246) * mm, "end": v(133, 250) * mm});
            skLineSegment(sketch, "E237.MirrorCS", {"start": v(100, 250) * mm, "end": v(100, 254) * mm});
            skLineSegment(sketch, "E238.MirrorCS", {"start": v(140, 250) * mm, "end": v(140, 254) * mm});
            skLineSegment(sketch, "E239.MirrorCS", {"start": v(93.4, 242) * mm, "end": v(95, 243.6) * mm});
            skLineSegment(sketch, "E240.MirrorCS", {"start": v(173.4, 242) * mm, "end": v(175, 243.6) * mm});
            skLineSegment(sketch, "E241.MirrorCS", {"start": v(125, 243.6) * mm, "end": v(125, 246) * mm});
            skLineSegment(sketch, "E242.MirrorCS", {"start": v(247, 246) * mm, "end": v(247, 250) * mm});
            skLineSegment(sketch, "E243.MirrorCS", {"start": v(90, 242) * mm, "end": v(86.6, 242) * mm});
            skLineSegment(sketch, "E244.MirrorCS", {"start": v(210, 242) * mm, "end": v(206.6, 242) * mm});
            skLineSegment(sketch, "E245.MirrorCS", {"start": v(200, 250) * mm, "end": v(200, 254) * mm});
            skLineSegment(sketch, "E246.MirrorCS", {"start": v(250, 242) * mm, "end": v(253.4, 242) * mm});
            skLineSegment(sketch, "E247.MirrorCS", {"start": v(90, 242) * mm, "end": v(93.4, 242) * mm});
            skLineSegment(sketch, "E248.MirrorCS", {"start": v(87, 250) * mm, "end": v(80, 250) * mm});
            skLineSegment(sketch, "E249.MirrorCS", {"start": v(240, 250) * mm, "end": v(240, 254) * mm});
            skLineSegment(sketch, "E250.MirrorCS", {"start": v(60, 250) * mm, "end": v(53, 250) * mm});
            skLineSegment(sketch, "E251.MirrorCS", {"start": v(245, 246) * mm, "end": v(247, 246) * mm});
            skLineSegment(sketch, "E252.MirrorCS", {"start": v(293, 246) * mm, "end": v(293, 250) * mm});
            skLineSegment(sketch, "E253.MirrorCS", {"start": v(45, 243.6) * mm, "end": v(45, 246) * mm});
            skLineSegment(sketch, "E254.MirrorCS", {"start": v(246.6, 242) * mm, "end": v(245, 243.6) * mm});
            skLineSegment(sketch, "E255.MirrorCS", {"start": v(125, 246) * mm, "end": v(127, 246) * mm});
            skLineSegment(sketch, "E256.MirrorCS", {"start": v(87, 246) * mm, "end": v(87, 250) * mm});
            skLineSegment(sketch, "E257.MirrorCS", {"start": v(250, 242) * mm, "end": v(246.6, 242) * mm});
            skLineSegment(sketch, "E258.MirrorCS", {"start": v(207, 250) * mm, "end": v(200, 250) * mm});
            skLineSegment(sketch, "E259.MirrorCS", {"start": v(206.6, 242) * mm, "end": v(205, 243.6) * mm});
            skLineSegment(sketch, "E260.MirrorCS", {"start": v(245, 243.6) * mm, "end": v(245, 246) * mm});
            skLineSegment(sketch, "E261.MirrorCS", {"start": v(100, 250) * mm, "end": v(93, 250) * mm});
            skLineSegment(sketch, "E262.MirrorCS", {"start": v(207, 246) * mm, "end": v(207, 250) * mm});
            skLineSegment(sketch, "E263.MirrorCS", {"start": v(280, 250) * mm, "end": v(280, 254) * mm});
            skLineSegment(sketch, "E264.MirrorCS", {"start": v(120, 250) * mm, "end": v(120, 254) * mm});
            skLineSegment(sketch, "E265.MirrorCS", {"start": v(85, 246) * mm, "end": v(87, 246) * mm});
            skLineSegment(sketch, "E266.MirrorCS", {"start": v(80, 250) * mm, "end": v(80, 254) * mm});
            skLineSegment(sketch, "E267.MirrorCS", {"start": v(260, 250) * mm, "end": v(253, 250) * mm});
            skLineSegment(sketch, "E268.MirrorCS", {"start": v(53.4, 242) * mm, "end": v(55, 243.6) * mm});
            skLineSegment(sketch, "E269.MirrorCS", {"start": v(50, 242) * mm, "end": v(46.6, 242) * mm});
            skLineSegment(sketch, "E270.MirrorCS", {"start": v(45, 246) * mm, "end": v(47, 246) * mm});
            skLineSegment(sketch, "E271.MirrorCS", {"start": v(300, 250) * mm, "end": v(300, 254) * mm});
            skLineSegment(sketch, "E272.MirrorCS", {"start": v(127, 246) * mm, "end": v(127, 250) * mm});
            skLineSegment(sketch, "E273.MirrorCS", {"start": v(160, 250) * mm, "end": v(160, 254) * mm});
            skLineSegment(sketch, "E274.MirrorCS", {"start": v(300, 250) * mm, "end": v(293, 250) * mm});
            skLineSegment(sketch, "E275.MirrorCS", {"start": v(50, 242) * mm, "end": v(53.4, 242) * mm});
            skLineSegment(sketch, "E276.MirrorCS", {"start": v(167, 250) * mm, "end": v(160, 250) * mm});
            skLineSegment(sketch, "E277.MirrorCS", {"start": v(93, 246) * mm, "end": v(93, 250) * mm});
            skLineSegment(sketch, "E278.MirrorCS", {"start": v(95, 246) * mm, "end": v(93, 246) * mm});
            skLineSegment(sketch, "E279.MirrorCS", {"start": v(210, 242) * mm, "end": v(213.4, 242) * mm});
            skLineSegment(sketch, "E280.MirrorCS", {"start": v(47, 246) * mm, "end": v(47, 250) * mm});
            skLineSegment(sketch, "E281.MirrorCS", {"start": v(166.6, 242) * mm, "end": v(165, 243.6) * mm});
            skLineSegment(sketch, "E282.MirrorCS", {"start": v(47, 250) * mm, "end": v(40, 250) * mm});
            skLineSegment(sketch, "E283.MirrorCS", {"start": v(127, 250) * mm, "end": v(120, 250) * mm});
            skLineSegment(sketch, "E284.MirrorCS", {"start": v(80, 254) * mm, "end": v(60, 254) * mm});
            skLineSegment(sketch, "E285.MirrorCS", {"start": v(280, 254) * mm, "end": v(260, 254) * mm});
            skLineSegment(sketch, "E286.MirrorCS", {"start": v(320, 254) * mm, "end": v(300, 254) * mm});
            skLineSegment(sketch, "E287.MirrorCS", {"start": v(120, 254) * mm, "end": v(100, 254) * mm});
            skPoint(sketch, "E288.MirrorP", {"position": v(262.25, 250) * mm});
            skLineSegment(sketch, "E289.MirrorCS", {"start": v(247, 250) * mm, "end": v(240, 250) * mm});
            skLineSegment(sketch, "E290.MirrorCS", {"start": v(160, 254) * mm, "end": v(140, 254) * mm});
            skLineSegment(sketch, "E291.MirrorCS", {"start": v(240, 254) * mm, "end": v(220, 254) * mm});
            skLineSegment(sketch, "E292.MirrorCS", {"start": v(200, 254) * mm, "end": v(180, 254) * mm});
            skLineSegment(sketch, "E293.MirrorCS", {"start": v(320, 250) * mm, "end": v(320, 254) * mm});
            skLineSegment(sketch, "E294", {"start": v(-40, 250) * mm, "end": v(40, 250) * mm});
            skSolve(sketch);
        }
        {
            var Q0;
            Q0=makeQuery(id+"F0.imprint","IMPRINT",FACE,{"disambiguationData":[TD([[makeQuery(id+"F0.imprint","IMPRINT",EDGE,{"derivedFrom":sQuery(id+"F0.wireOp",EDGE,"E0.top")}),1.0]])]});
            var Q1;
            Q1=makeQuery(id+"F0.imprint","IMPRINT",FACE,{"disambiguationData":[TD([[makeQuery(id+"F0.imprint","IMPRINT",EDGE,{"derivedFrom":sQuery(id+"F0.wireOp",EDGE,"E45.top")}),-1.0]])]});
            var Q2;
            {var subQ0=sQuery(id+"F0.wireOp",EDGE,"14073c0c-dfe3-492f-9f82-ccab3eef84c7.1.0.0");Q2=makeQuery(id+"F0.imprint","IMPRINT",FACE,{"disambiguationData":[TD([[makeQuery(id+"F0.imprint","IMPRINT",EDGE,{"derivedFrom":subQ0}),-1.0]])]});}
            var Q3;
            {var subQ0=sQuery(id+"F0.wireOp",EDGE,"14073c0c-dfe3-492f-9f82-ccab3eef84c7.2.0.0");Q3=makeQuery(id+"F0.imprint","IMPRINT",FACE,{"disambiguationData":[TD([[makeQuery(id+"F0.imprint","IMPRINT",EDGE,{"derivedFrom":subQ0}),-1.0]])]});}
            var Q4;
            {var subQ0=sQuery(id+"F0.wireOp",EDGE,"14073c0c-dfe3-492f-9f82-ccab3eef84c7.3.0.0");Q4=makeQuery(id+"F0.imprint","IMPRINT",FACE,{"disambiguationData":[TD([[makeQuery(id+"F0.imprint","IMPRINT",EDGE,{"derivedFrom":subQ0}),-1.0]])]});}
            var Q5;
            {var subQ0=sQuery(id+"F0.wireOp",EDGE,"14073c0c-dfe3-492f-9f82-ccab3eef84c7.4.0.0");Q5=makeQuery(id+"F0.imprint","IMPRINT",FACE,{"disambiguationData":[TD([[makeQuery(id+"F0.imprint","IMPRINT",EDGE,{"derivedFrom":subQ0}),-1.0]])]});}
            var Q6;
            {var subQ0=sQuery(id+"F0.wireOp",EDGE,"14073c0c-dfe3-492f-9f82-ccab3eef84c7.5.0.0");Q6=makeQuery(id+"F0.imprint","IMPRINT",FACE,{"disambiguationData":[TD([[makeQuery(id+"F0.imprint","IMPRINT",EDGE,{"derivedFrom":subQ0}),-1.0]])]});}
            var Q7;
            {var subQ0=sQuery(id+"F0.wireOp",EDGE,"14073c0c-dfe3-492f-9f82-ccab3eef84c7.6.0.0");Q7=makeQuery(id+"F0.imprint","IMPRINT",FACE,{"disambiguationData":[TD([[makeQuery(id+"F0.imprint","IMPRINT",EDGE,{"derivedFrom":subQ0}),-1.0]])]});}
            var Q8;
            {var subQ0=sQuery(id+"F0.wireOp",EDGE,"84a22808-81aa-497e-832c-de5d24872d6718.MirrorCS");Q8=makeQuery(id+"F0.imprint","IMPRINT",FACE,{"disambiguationData":[TD([[makeQuery(id+"F0.imprint","IMPRINT",EDGE,{"derivedFrom":subQ0}),1.0]])]});}
            var Q9;
            {var subQ0=sQuery(id+"F0.wireOp",EDGE,"84a22808-81aa-497e-832c-de5d24872d6724.MirrorCS");Q9=makeQuery(id+"F0.imprint","IMPRINT",FACE,{"disambiguationData":[TD([[makeQuery(id+"F0.imprint","IMPRINT",EDGE,{"derivedFrom":subQ0}),-1.0]])]});}
            var Q10;
            {var subQ2=sQuery(id+"F0.wireOp",EDGE,"84a22808-81aa-497e-832c-de5d24872d673.MirrorCS");Q10=makeQuery(id+"F0.imprint","IMPRINT",FACE,{"disambiguationData":[TD([[makeQuery(id+"F0.imprint","IMPRINT",EDGE,{"derivedFrom":subQ2}),-1.0]])]});}
            var Q11;
            {var subQ0=sQuery(id+"F0.wireOp",EDGE,"84a22808-81aa-497e-832c-de5d24872d675.MirrorCS");Q11=makeQuery(id+"F0.imprint","IMPRINT",FACE,{"disambiguationData":[TD([[makeQuery(id+"F0.imprint","IMPRINT",EDGE,{"derivedFrom":subQ0}),1.0]])]});}
            var Q12;
            {var subQ0=sQuery(id+"F0.wireOp",EDGE,"84a22808-81aa-497e-832c-de5d24872d6714.MirrorCS");Q12=makeQuery(id+"F0.imprint","IMPRINT",FACE,{"disambiguationData":[TD([[makeQuery(id+"F0.imprint","IMPRINT",EDGE,{"derivedFrom":subQ0}),-1.0]])]});}
            var Q13;
            {var subQ0=sQuery(id+"F0.wireOp",EDGE,"84a22808-81aa-497e-832c-de5d24872d6721.MirrorCS");Q13=makeQuery(id+"F0.imprint","IMPRINT",FACE,{"disambiguationData":[TD([[makeQuery(id+"F0.imprint","IMPRINT",EDGE,{"derivedFrom":subQ0}),1.0]])]});}
            var Q14;
            {var subQ0=sQuery(id+"F0.wireOp",EDGE,"84a22808-81aa-497e-832c-de5d24872d6734.MirrorCS");Q14=makeQuery(id+"F0.imprint","IMPRINT",FACE,{"disambiguationData":[TD([[makeQuery(id+"F0.imprint","IMPRINT",EDGE,{"derivedFrom":subQ0}),1.0]])]});}
            extrude(context, id + "F1", {"entities" : qUnion([Q0, Q1, Q2, Q3, Q4, Q5, Q6, Q7, Q8, Q9, Q10, Q11, Q12, Q13, Q14]), "depth" : 4 * mm, "offsetDistance" : 25 * mm});
        }
    });
